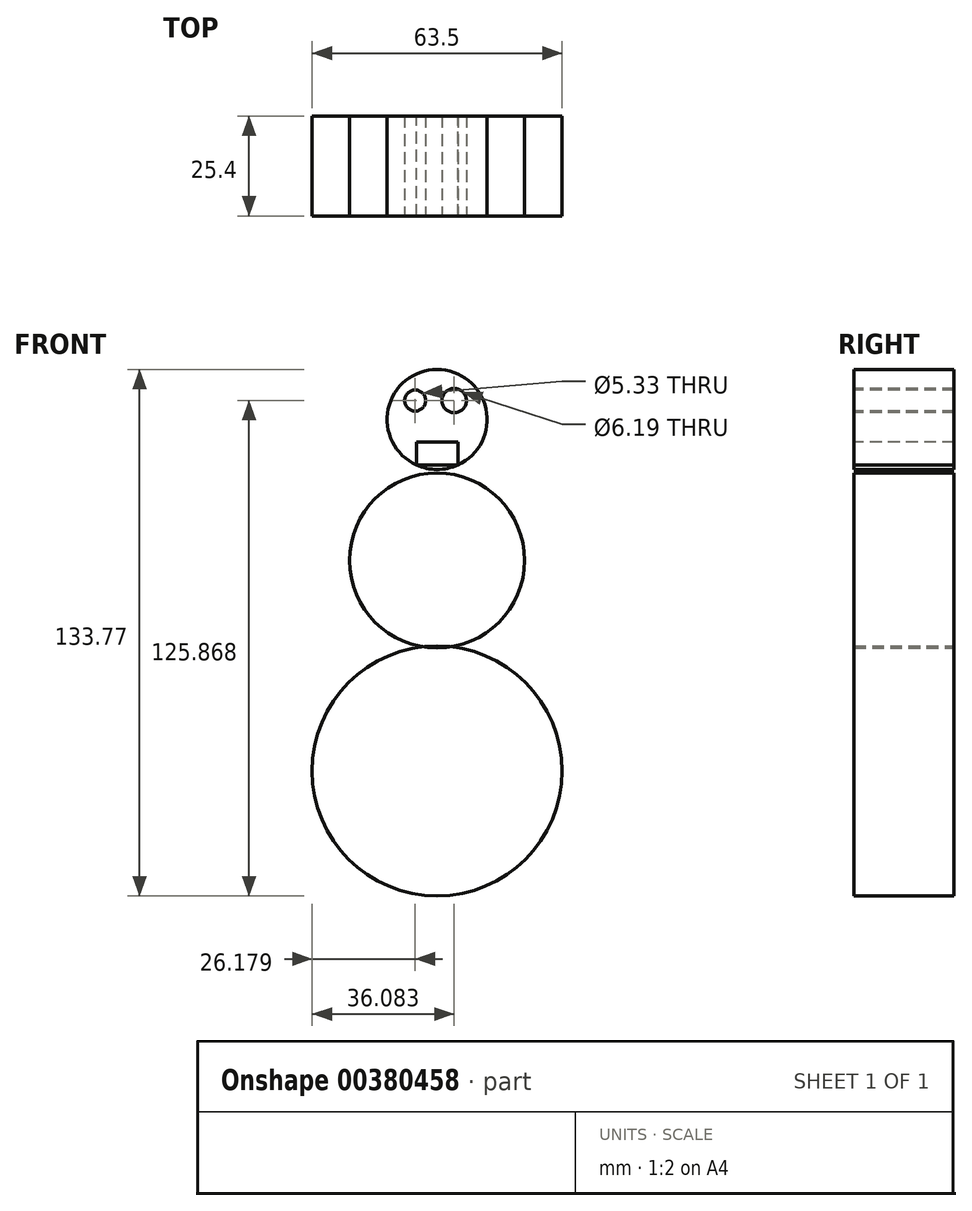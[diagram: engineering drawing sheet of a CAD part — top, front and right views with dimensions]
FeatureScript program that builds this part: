
annotation { "Feature Type Name" : "Feature", "Feature Type Description" : "" }
export const myFeature = defineFeature(function(context is Context, id is Id, definition is map)
    precondition{}
    {
        {
            var Q0;
            Q0=qCreatedBy(makeId("Front.planeOp"),FACE);
            var sketch = newSketch(context, id + "F0", { "sketchPlane" : qUnion([Q0])});
            skCircle(sketch, "E0", {"center": v(0, -31.75) * mm, "radius": 31.75 * mm});
            skSolve(sketch);
        }
        {
            var Q0;
            Q0 = qSketchRegion(id + "F0", true);
            extrude(context, id + "F1", {"entities" : qUnion([Q0]), "depth" : 25.4 * mm});
        }
        {
            var Q0;
            Q0=qCreatedBy(makeId("Front.planeOp"),FACE);
            var sketch = newSketch(context, id + "F2", { "sketchPlane" : qUnion([Q0])});
            skCircle(sketch, "E1", {"center": v(0, 21.76) * mm, "radius": 22.23 * mm});
            skCircle(sketch, "E2", {"center": v(0, 57.57) * mm, "radius": 12.7 * mm});
            skSolve(sketch);
        }
        {
            var Q0;
            Q0=makeQuery(id+"F2.imprint","IMPRINT",FACE,{"disambiguationData":[TD([[makeQuery(id+"F2.imprint","IMPRINT",EDGE,{"derivedFrom":sQuery(id+"F2.wireOp",EDGE,"E1")}),1.0]])]});
            var Q1;
            Q1=makeQuery(id+"F2.imprint","IMPRINT",FACE,{"disambiguationData":[TD([[makeQuery(id+"F2.imprint","IMPRINT",EDGE,{"derivedFrom":sQuery(id+"F2.wireOp",EDGE,"E2")}),1.0]])]});
            extrude(context, id + "F3", {"entities" : qUnion([Q0, Q1]), "depth" : 25.4 * mm});
        }
        {
            var Q0;
            Q0=makeQuery(id+"F3.opExtrude","CAP_FACE",FACE,{"disambiguationData":[OSD([sQuery(id+"F2.wireOp",EDGE,"E2")])],"isStart":false});
            var sketch = newSketch(context, id + "F4", { "sketchPlane" : qUnion([Q0])});
            skCircle(sketch, "E3", {"center": v(-5.57, 62.37) * mm, "radius": 2.66 * mm});
            skCircle(sketch, "E4", {"center": v(4.33, 62.37) * mm, "radius": 3.1 * mm});
            skSolve(sketch);
        }
        {
            var Q0;
            Q0=makeQuery(id+"F4.imprint","IMPRINT",FACE,{"disambiguationData":[TD([[makeQuery(id+"F4.imprint","IMPRINT",EDGE,{"derivedFrom":sQuery(id+"F4.wireOp",EDGE,"E4")}),1.0]])]});
            var Q1;
            Q1=makeQuery(id+"F4.imprint","IMPRINT",FACE,{"disambiguationData":[TD([[makeQuery(id+"F4.imprint","IMPRINT",EDGE,{"derivedFrom":sQuery(id+"F4.wireOp",EDGE,"E3")}),1.0]])]});
            extrude(context, id + "F5", {"entities" : qUnion([Q0, Q1]), "operationType" : NewBodyOperationType.REMOVE, "oppositeDirection" : true, "depth" : 25.4 * mm});
        }
        {
            var Q0;
            Q0=makeQuery(id+"F3.opExtrude","CAP_FACE",FACE,{"disambiguationData":[OSD([sQuery(id+"F2.wireOp",EDGE,"E2")])],"isStart":false});
            var sketch = newSketch(context, id + "F6", { "sketchPlane" : qUnion([Q0])});
            skLineSegment(sketch, "E5", {"start": v(-5.27, 51.87) * mm, "end": v(5.25, 51.87) * mm});
            skLineSegment(sketch, "E6", {"start": v(-5.27, 51.87) * mm, "end": v(-5.27, 46.01) * mm});
            skLineSegment(sketch, "E7", {"start": v(-5.27, 46.01) * mm, "end": v(5.27, 46.01) * mm});
            skLineSegment(sketch, "E8", {"start": v(5.27, 46.01) * mm, "end": v(5.25, 51.87) * mm});
            skSolve(sketch);
        }
        {
            var Q0;
            Q0=makeQuery(id+"F6.imprint","IMPRINT",FACE,{"disambiguationData":[TD([[makeQuery(id+"F6.imprint","IMPRINT",EDGE,{"derivedFrom":sQuery(id+"F6.wireOp",EDGE,"E5")}),-1.0]])]});
            extrude(context, id + "F7", {"entities" : qUnion([Q0]), "operationType" : NewBodyOperationType.REMOVE, "oppositeDirection" : true, "depth" : 25.4 * mm});
        }
    });
